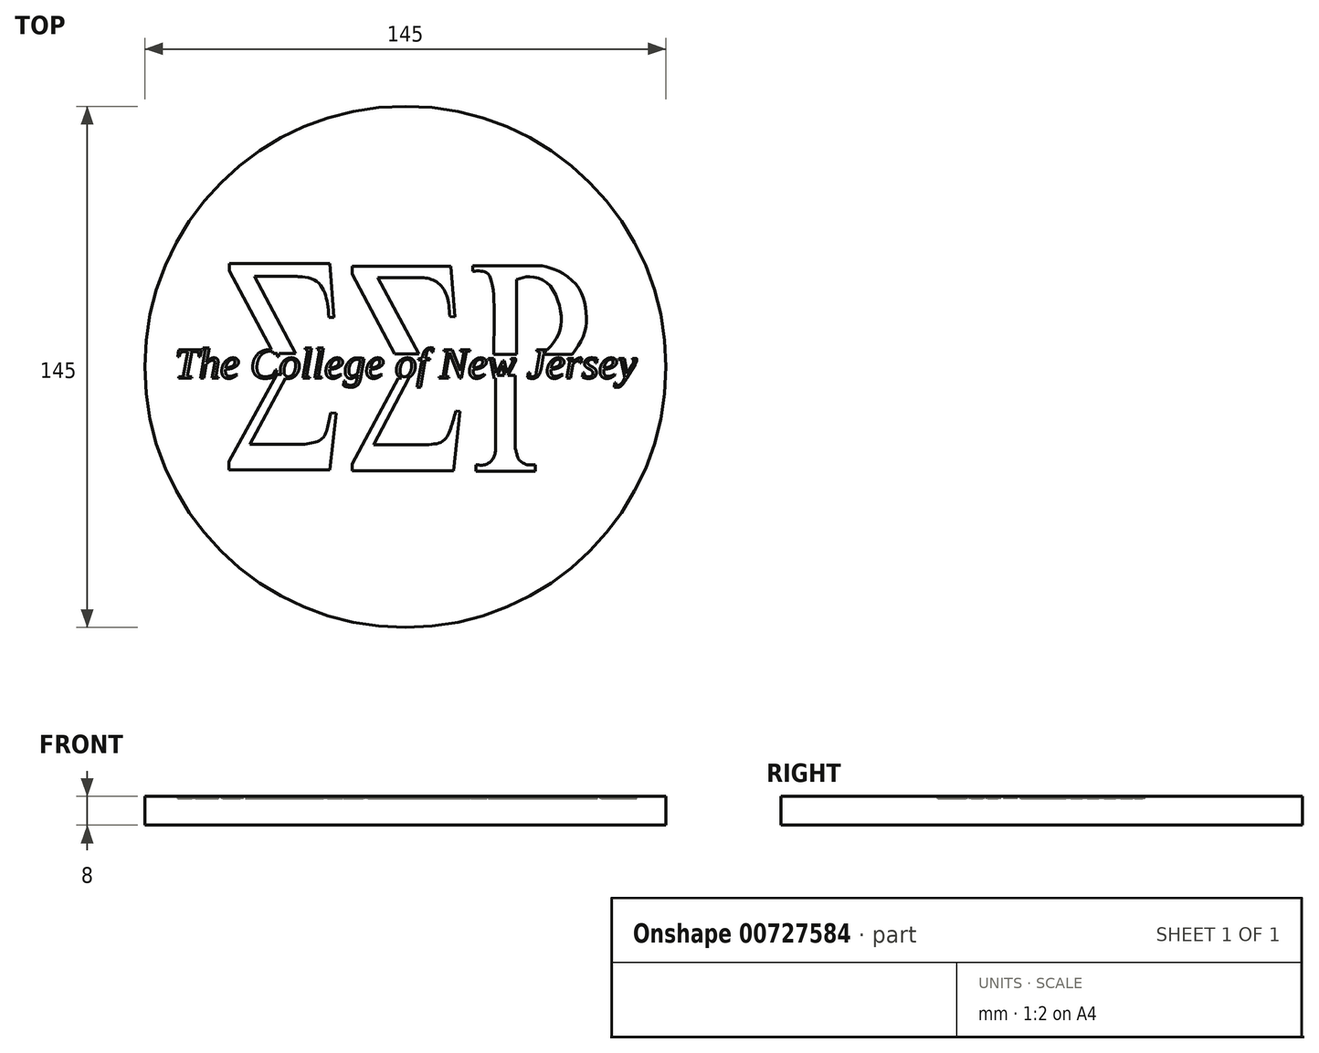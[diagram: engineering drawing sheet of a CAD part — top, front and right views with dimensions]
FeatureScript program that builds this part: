
annotation { "Feature Type Name" : "Feature", "Feature Type Description" : "" }
export const myFeature = defineFeature(function(context is Context, id is Id, definition is map)
    precondition{}
    {
        {
            var Q0;
            Q0=qCreatedBy(makeId("Top.planeOp"),FACE);
            var sketch = newSketch(context, id + "F0", { "sketchPlane" : qUnion([Q0])});
            skCircle(sketch, "E0", {"center": v(0, 0) * mm, "radius": 72.5 * mm});
            skSolve(sketch);
        }
        {
            var Q0;
            Q0=makeQuery(id+"F0.imprint","IMPRINT",FACE,{"disambiguationData":[TD([[makeQuery(id+"F0.imprint","IMPRINT",EDGE,{"derivedFrom":sQuery(id+"F0.wireOp",EDGE,"E0")}),1.0]])]});
            var Q1;
            Q1=sQuery(id+"F0.wireOp",EDGE,"E0");
            extrude(context, id + "F1", {"entities" : qUnion([Q0]), "surfaceEntities" : qUnion([Q1]), "depth" : 8 * mm, "offsetDistance" : 25.4 * mm});
        }
        {
            var Q0;
            Q0=makeQuery(id+"F1.opExtrude","CAP_FACE",FACE,{"disambiguationData":[OSD([sQuery(id+"F0.wireOp",EDGE,"E0")])],"isStart":false});
            var sketch = newSketch(context, id + "F2", { "sketchPlane" : qUnion([Q0])});
            skLineSegment(sketch, "E1", {"start": v(-48.94, 28.72) * mm, "end": v(-20.98, 28.72) * mm});
            skLineSegment(sketch, "E2", {"start": v(-20.98, 28.72) * mm, "end": v(-19.84, 13.76) * mm});
            skLineSegment(sketch, "E3", {"start": v(-19.84, 13.76) * mm, "end": v(-21.3, 13.76) * mm});
            skLineSegment(sketch, "E4", {"start": v(-48.94, 28.72) * mm, "end": v(-48.94, 26.77) * mm});
            skLineSegment(sketch, "E5", {"start": v(-48.94, 26.77) * mm, "end": v(-36.75, 3.69) * mm});
            skLineSegment(sketch, "E6", {"start": v(-36.75, 3.69) * mm, "end": v(-30.57, 3.69) * mm});
            skLineSegment(sketch, "E7", {"start": v(-30.57, 3.69) * mm, "end": v(-41.96, 25.14) * mm});
            skLineSegment(sketch, "E8", {"start": v(-41.96, 25.14) * mm, "end": v(-30.57, 25.14) * mm});
            skFitSpline(sketch, "E9", {"points": [v(-30.57, 25.14) * mm, v(-30.08, 25.14) * mm, v(-26.02, 24.5) * mm, v(-22.44, 20.6) * mm, v(-21.3, 13.76) * mm], "startDerivative": vector(18.68, 2.6) * mm, "endDerivative": vector(1.71, -24.05) * mm});
            skLineSegment(sketch, "E10", {"start": v(-35.77, -2.16) * mm, "end": v(-32.85, -2.16) * mm});
            skLineSegment(sketch, "E11", {"start": v(-32.85, -2.16) * mm, "end": v(-43.25, -21.5) * mm});
            skLineSegment(sketch, "E12", {"start": v(-43.25, -21.5) * mm, "end": v(-27.97, -21.5) * mm});
            skLineSegment(sketch, "E13", {"start": v(-35.77, -2.16) * mm, "end": v(-49.1, -26.38) * mm});
            skLineSegment(sketch, "E14", {"start": v(-49.1, -26.38) * mm, "end": v(-49.1, -28.66) * mm});
            skLineSegment(sketch, "E15", {"start": v(-49.1, -28.66) * mm, "end": v(-20.98, -28.66) * mm});
            skLineSegment(sketch, "E16", {"start": v(-20.98, -28.66) * mm, "end": v(-19.2, -12.9) * mm});
            skLineSegment(sketch, "E17", {"start": v(-19.2, -12.9) * mm, "end": v(-20.75, -12.72) * mm});
            skFitSpline(sketch, "E18", {"points": [v(-20.75, -12.72) * mm, v(-21.83, -17.46) * mm, v(-23.52, -20.24) * mm, v(-27.97, -21.5) * mm], "startDerivative": vector(-2.7, -13.96) * mm, "endDerivative": vector(-14.58, -2.2) * mm});
            skLineSegment(sketch, "E19", {"start": v(-1.97, -3.12) * mm, "end": v(0.96, -3.12) * mm});
            skLineSegment(sketch, "E20", {"start": v(0.96, -3.12) * mm, "end": v(-8.82, -21.68) * mm});
            skLineSegment(sketch, "E21", {"start": v(-8.82, -21.68) * mm, "end": v(5.01, -21.68) * mm});
            skLineSegment(sketch, "E22", {"start": v(-1.97, -3.12) * mm, "end": v(-14.8, -27.04) * mm});
            skLineSegment(sketch, "E23", {"start": v(-14.8, -27.04) * mm, "end": v(-14.8, -28.85) * mm});
            skLineSegment(sketch, "E24", {"start": v(-14.8, -28.85) * mm, "end": v(13.43, -28.85) * mm});
            skLineSegment(sketch, "E25", {"start": v(13.43, -28.85) * mm, "end": v(15.11, -12.4) * mm});
            skLineSegment(sketch, "E26", {"start": v(15.11, -12.4) * mm, "end": v(14.01, -12.28) * mm});
            skFitSpline(sketch, "E27", {"points": [v(14.01, -12.28) * mm, v(12.68, -16.88) * mm, v(10.5, -20.62) * mm, v(5.01, -21.68) * mm], "startDerivative": vector(-3.78, -13.92) * mm, "endDerivative": vector(-17.57, -0.59) * mm});
            skLineSegment(sketch, "E28", {"start": v(-3.04, 3.57) * mm, "end": v(-14.75, 25.81) * mm});
            skLineSegment(sketch, "E29", {"start": v(-14.75, 25.81) * mm, "end": v(-14.75, 28.04) * mm});
            skLineSegment(sketch, "E30", {"start": v(-14.75, 28.04) * mm, "end": v(12.68, 28.04) * mm});
            skLineSegment(sketch, "E31", {"start": v(12.68, 28.04) * mm, "end": v(13.72, 13.95) * mm});
            skLineSegment(sketch, "E32", {"start": v(-3.04, 3.57) * mm, "end": v(3.71, 3.57) * mm});
            skLineSegment(sketch, "E33", {"start": v(3.71, 3.57) * mm, "end": v(-7.68, 24.84) * mm});
            skLineSegment(sketch, "E34", {"start": v(-7.68, 24.84) * mm, "end": v(5.15, 24.84) * mm});
            skFitSpline(sketch, "E35", {"points": [v(5.15, 24.84) * mm, v(8.5, 23.76) * mm, v(11.26, 20.4) * mm, v(12.34, 14.05) * mm], "startDerivative": vector(12.05, -2.37) * mm, "endDerivative": vector(1.3, -17.45) * mm});
            skLineSegment(sketch, "E36", {"start": v(13.72, 13.95) * mm, "end": v(12.34, 14.05) * mm});
            skLineSegment(sketch, "E37", {"start": v(18.72, 28.05) * mm, "end": v(18.72, 26.58) * mm});
            skFitSpline(sketch, "E38", {"points": [v(18.72, 26.58) * mm, v(21.46, 26.58) * mm, v(23.57, 24.9) * mm, v(24.51, 3.52) * mm], "startDerivative": vector(13.58, 1.14) * mm, "endDerivative": vector(-1.35, -46.7) * mm});
            skLineSegment(sketch, "E39", {"start": v(24.51, 3.52) * mm, "end": v(30.94, 3.52) * mm});
            skLineSegment(sketch, "E40", {"start": v(30.94, 3.52) * mm, "end": v(30.94, 24.26) * mm});
            skLineSegment(sketch, "E41", {"start": v(18.72, 28.05) * mm, "end": v(38, 28.05) * mm});
            skFitSpline(sketch, "E42", {"points": [v(38, 28.05) * mm, v(42.83, 26.58) * mm, v(48.3, 21.74) * mm, v(50.2, 15.63) * mm, v(49.78, 9.42) * mm, v(46.41, 3.52) * mm], "startDerivative": vector(26.54, -5.23) * mm, "endDerivative": vector(-19.59, -27.7) * mm});
            skLineSegment(sketch, "E43", {"start": v(46.41, 3.52) * mm, "end": v(38.3, 3.52) * mm});
            skFitSpline(sketch, "E44", {"points": [v(30.94, 24.26) * mm, v(34.2, 25.1) * mm, v(39.57, 23.2) * mm, v(43.15, 15.63) * mm, v(42.62, 9.1) * mm, v(38.3, 3.52) * mm], "startDerivative": vector(20.07, 7.99) * mm, "endDerivative": vector(-23.86, -24.83) * mm});
            skLineSegment(sketch, "E45", {"start": v(25.1, -2.35) * mm, "end": v(30.55, -2.35) * mm});
            skLineSegment(sketch, "E46", {"start": v(30.55, -2.35) * mm, "end": v(30.55, -22.68) * mm});
            skLineSegment(sketch, "E47", {"start": v(25.1, -2.35) * mm, "end": v(25.1, -22.76) * mm});
            skLineSegment(sketch, "E48", {"start": v(19.67, -27.2) * mm, "end": v(19.67, -28.98) * mm});
            skLineSegment(sketch, "E49", {"start": v(19.67, -28.98) * mm, "end": v(36.06, -28.98) * mm});
            skLineSegment(sketch, "E50", {"start": v(36.06, -28.98) * mm, "end": v(36.06, -27.2) * mm});
            skFitSpline(sketch, "E51", {"points": [v(19.67, -27.2) * mm, v(22.32, -27.2) * mm, v(24.46, -25.33) * mm, v(25.1, -22.76) * mm], "startDerivative": vector(8.22, -1.28) * mm, "endDerivative": vector(0.93, 8.07) * mm});
            skFitSpline(sketch, "E52", {"points": [v(36.06, -27.2) * mm, v(33.77, -27.2) * mm, v(31.62, -25.9) * mm, v(31.05, -24.47) * mm, v(30.55, -22.68) * mm], "startDerivative": vector(-8.48, -1.1) * mm, "endDerivative": vector(-2.27, 7.69) * mm});
            skText(sketch, "E53", { "text": "The College of New Jersey", "fontName": "Tinos-Italic.ttf"});
            const initialGuessF2  = {"E53": [-0.06412, -0.00312, 1, 0, 0.00863]};
            skSetInitialGuess(sketch, initialGuessF2);
            skSolve(sketch);
        }
        {
            var Q0;
            Q0 = qSketchRegion(id + "F2", true);
            extrude(context, id + "F3", {"entities" : qUnion([Q0]), "operationType" : NewBodyOperationType.REMOVE, "oppositeDirection" : true, "depth" : 0.64 * mm, "offsetDistance" : 25.4 * mm});
        }
    });
